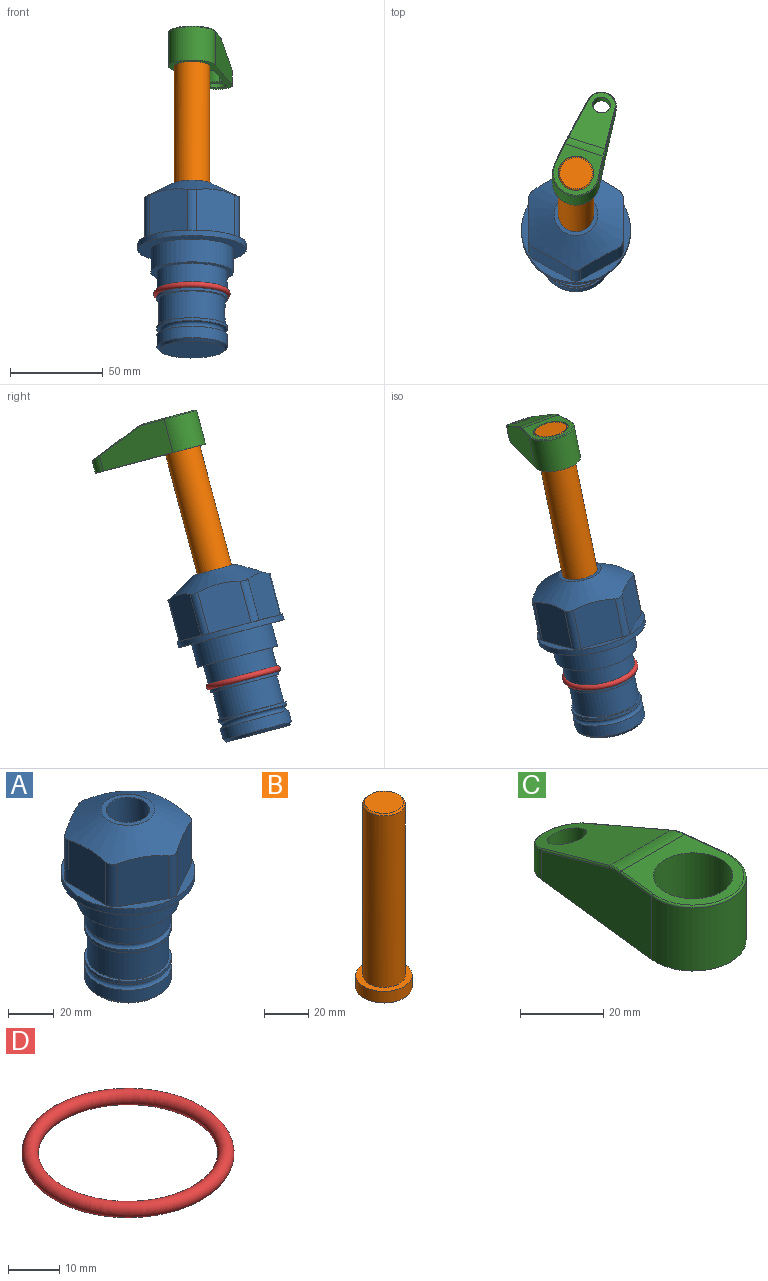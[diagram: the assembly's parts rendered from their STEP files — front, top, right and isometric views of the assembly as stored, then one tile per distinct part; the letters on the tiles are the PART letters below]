
ASSEMBLY  parts=4 mates=2
PART A: 36 faces, bbox 58.7x58.7x91.2 mm
  f0: cylinder r=17.78mm len=35.56mm, axis (0,0,1), area 1670.8mm2, adj f23,f24,f31
  f1: cylinder r=19.05mm len=38.1mm, axis (0,0,1), area 1191.9mm2, adj f26,f27,f30
  f2: plane 58.66x58.66mm, normal (0,0,-1), area 1150.6mm2, adj f3,f28
  f3: cylinder r=29.33mm len=58.66mm, axis (0,0,-1), area 585.1mm2, adj f2,f4
  f4: plane 58.66x58.66mm, normal (0,0,1), area 475.9mm2, adj f3,f5,f6,f7,f8,f9,f10,f11
  f5: plane 24.5x20.32mm, normal (-0.5,0.87,0), area 562.8mm2, adj f4,f15,f16,f17
  f6: plane 24.5x20.32mm, normal (0.5,0.87,0), area 562.8mm2, adj f4,f14,f15,f17
  f7: plane 24.5x23.48mm, normal (1,0,0), area 562.8mm2, adj f4,f13,f14,f17
  f8: plane 24.5x20.32mm, normal (0.5,-0.87,0), area 562.8mm2, adj f4,f12,f13,f17
  f9: plane 24.5x20.32mm, normal (-0.5,-0.87,0), area 562.8mm2, adj f4,f11,f12,f17
  f10: plane 24.5x23.48mm, normal (-1,0,0), area 562.8mm2, adj f4,f11,f16,f17
  f11: cylinder r=5.08mm len=23.01mm, axis (0,0,-1), area 121.2mm2, adj f4,f9,f10,f17
  f12: cylinder r=5.08mm len=23.01mm, axis (0,0,-1), area 121.2mm2, adj f4,f8,f9,f17
  f13: cylinder r=5.08mm len=23.01mm, axis (0,0,-1), area 121.2mm2, adj f4,f7,f8,f17
  f14: cylinder r=5.08mm len=23.01mm, axis (0,0,-1), area 121.2mm2, adj f4,f6,f7,f17
  f15: cylinder r=5.08mm len=23.01mm, axis (0,0,-1), area 121.2mm2, adj f4,f5,f6,f17
  f16: cylinder r=5.08mm len=23.01mm, axis (0,0,-1), area 121.2mm2, adj f4,f5,f10,f17
  f17: cone r=11.73mm half-angle=60deg, axis (0,0,-1), area 2071.8mm2, adj f5,f6,f7,f8,f9,f10,f11,f12
  f18: plane 23.46x23.46mm, normal (0,0,1), area 147.4mm2, adj f17,f35
  f19: plane 34.93x34.93mm, normal (0,0,-1), area 958mm2, adj f29
  f20: cylinder r=19.05mm len=38.1mm, axis (0,0,1), area 760.1mm2, adj f21,f29
  f21: torus R=19.05mm, axis (0,0,1), area 565.3mm2, adj f20,f22
  f22: cylinder r=19.05mm len=38.1mm, axis (0,0,1), area 190mm2, adj f21,f23
  f23: plane 38.1x38.1mm, normal (0,0,1), area 146.9mm2, adj f0,f22
  f24: plane 38.1x38.1mm, normal (0,0,-1), area 146.9mm2, adj f0,f25
  f25: cylinder r=19.05mm len=38.1mm, axis (0,0,1), area 190mm2, adj f24,f26
  f26: torus R=19.05mm, axis (0,0,1), area 565.3mm2, adj f1,f25
  f27: plane 44.45x44.45mm, normal (0,0,-1), area 411.7mm2, adj f1,f28
  f28: cylinder r=22.23mm len=44.45mm, axis (0,0,1), area 1773.5mm2, adj f2,f27
  f29: cone r=19.05mm half-angle=45deg, axis (0,0,1), area 257.5mm2, adj f19,f20
  f30: cylinder r=3.17mm len=6.75mm, axis (-1,0,0), area 128mm2, adj f1,f33
  f31: cylinder r=3.17mm len=6.35mm, axis (-1,0,0), area 102.5mm2, adj f0,f33
  f32: plane 25.4x25.4mm, normal (0,0,1), area 506.7mm2, adj f33
  f33: cylinder r=12.7mm len=66.42mm, axis (0,0,-1), area 5236.2mm2, adj f30,f31,f32,f34
  f34: cone r=9.53mm half-angle=30deg, axis (0,0,-1), area 443.4mm2, adj f33,f35
  f35: cylinder r=9.53mm len=19.05mm, axis (0,0,-1), area 849mm2, adj f18,f34
PART B: 6 faces, bbox 25.4x25.4x101.6 mm
  f0: plane 17.46x17.46mm, normal (0,0,1), area 239.5mm2, adj f5
  f1: plane 25.4x25.4mm, normal (0,0,-1), area 506.7mm2, adj f2
  f2: cylinder r=12.7mm len=25.4mm, axis (0,0,1), area 506.7mm2, adj f1,f3
  f3: plane 25.4x25.4mm, normal (0,0,1), area 221.7mm2, adj f2,f4
  f4: cylinder r=9.53mm len=94.46mm, axis (0,0,1), area 5653mm2, adj f3,f5
  f5: cone r=8.73mm half-angle=45deg, axis (0,0,-1), area 64.4mm2, adj f0,f4
PART C: 44 faces, bbox 27.5x64.5x19.1 mm
  f0: plane 2.3x0.95mm, normal (0,0,-1), area 1mm2, adj f25,f30,f34
  f1: plane 63.5x25.4mm, normal (0,0,-1), area 561.7mm2, adj f2,f3,f4,f5,f6,f7,f19,f20
  f2: cylinder r=12.7mm len=25.4mm, axis (0,0,-1), area 792.2mm2, adj f1,f3,f5,f13
  f3: plane 42.33x18.54mm, normal (0.99,0.11,0), area 647mm2, adj f1,f2,f4,f11,f12,f14
  f4: cylinder r=7.94mm len=15.78mm, axis (0,0,-1), area 158.6mm2, adj f1,f3,f5,f16
  f5: plane 42.33x18.54mm, normal (-0.99,0.11,0), area 647mm2, adj f1,f2,f4,f15,f17,f18
  f6: cylinder r=9.53mm len=19.05mm, axis (0,0,-1), area 1140.1mm2, adj f1,f8
  f7: cylinder r=4.76mm len=10.98mm, axis (0,0,-1), area 276.1mm2, adj f1,f9
  f8: plane 25.83x24.38mm, normal (0,0,1), area 262.2mm2, adj f6,f10,f11,f13,f15
  f9: plane 32.49x20.55mm, normal (0,0.34,0.94), area 489.9mm2, adj f7,f10,f14,f16,f18
  f10: cylinder r=12.7mm len=21.49mm, axis (-1,0,0), area 93.2mm2, adj f8,f9,f12,f17
  f11: cylinder r=0.51mm len=12.34mm, axis (0.11,-0.99,0), area 9.9mm2, adj f3,f8,f12,f13
  f12: bspline ~7.62x1.64mm, area 3.5mm2, adj f3,f10,f11,f14
  f13: torus R=12.19mm, axis (0,0,1), area 33.6mm2, adj f2,f8,f11,f15
  f14: cylinder r=0.51mm len=26.01mm, axis (0.1,-0.93,0.34), area 21.6mm2, adj f3,f9,f12,f16
  f15: cylinder r=0.51mm len=12.34mm, axis (0.11,0.99,0), area 9.9mm2, adj f5,f8,f13,f17
  f16: bspline ~15.78x7.05mm, area 15.7mm2, adj f4,f9,f14,f18
  f17: bspline ~7.62x1.64mm, area 3.5mm2, adj f5,f10,f15,f18
  f18: cylinder r=0.51mm len=26.01mm, axis (0.1,0.93,-0.34), area 21.6mm2, adj f5,f9,f16,f17
  f19: plane 21.6x14.29mm, normal (-0.99,-0.11,0), area 242.6mm2, adj f1,f26,f28,f34,f36,f38
  f20: plane 21.6x14.29mm, normal (0.99,-0.11,0), area 242.6mm2, adj f1,f27,f29,f37,f39,f41
  f21: cylinder r=12.7mm len=14.29mm, axis (0,0,-1), area 173.2mm2, adj f1,f26,f27,f30,f31,f33
  f22: cylinder r=7.94mm len=7.63mm, axis (0,0,-1), area 53.8mm2, adj f1,f28,f29,f42
  f23: plane 2.3x0.95mm, normal (0,0,-1), area 1mm2, adj f25,f33,f37
  f24: plane 17.94x12.32mm, normal (0,-0.34,-0.94), area 191.2mm2, adj f25,f38,f41,f42
  f25: cylinder r=9.53mm len=12.93mm, axis (-1,0,0), area 37.5mm2, adj f0,f23,f24,f31,f36,f39
  f26: cylinder r=1.59mm len=14.29mm, axis (0,0,-1), area 49mm2, adj f1,f19,f21,f32
  f27: cylinder r=1.59mm len=14.29mm, axis (0,0,-1), area 49mm2, adj f1,f20,f21,f35
  f28: cylinder r=1.59mm len=7.28mm, axis (0,0,-1), area 22.1mm2, adj f1,f19,f22,f40
  f29: cylinder r=1.59mm len=7.28mm, axis (0,0,-1), area 22.1mm2, adj f1,f20,f22,f43
  f30: torus R=14.29mm, axis (0,0,1), area 5.8mm2, adj f0,f21,f31,f32
  f31: bspline ~11.06x2.73mm, area 20.8mm2, adj f21,f25,f30,f33
  f32: sphere r=1.59mm, area 5.4mm2, adj f26,f30,f34
  f33: torus R=14.29mm, axis (0,0,1), area 5.8mm2, adj f21,f23,f31,f35
  f34: cylinder r=1.59mm len=1.68mm, axis (-0.11,0.99,0), area 2.4mm2, adj f0,f19,f32,f36
  f35: sphere r=1.59mm, area 5.4mm2, adj f27,f33,f37
  f36: bspline ~5.82x2.33mm, area 7.7mm2, adj f19,f25,f34,f38
  f37: cylinder r=1.59mm len=1.68mm, axis (0.11,0.99,0), area 2.4mm2, adj f20,f23,f35,f39
  f38: cylinder r=1.59mm len=18.33mm, axis (0.1,-0.93,0.34), area 46.7mm2, adj f19,f24,f36,f40
  f39: bspline ~5.82x2.33mm, area 7.7mm2, adj f20,f25,f37,f41
  f40: sphere r=1.59mm, area 3.6mm2, adj f28,f38,f42
  f41: cylinder r=1.59mm len=18.33mm, axis (0.1,0.93,-0.34), area 46.7mm2, adj f20,f24,f39,f43
  f42: bspline ~8.31x1.84mm, area 15.3mm2, adj f22,f24,f40,f43
  f43: sphere r=1.59mm, area 3.6mm2, adj f29,f41,f42
PART D: 1 faces, bbox 44.7x44.7x3.2 mm
  f0: torus R=19.05mm, axis (0,0,1), area 1193.9mm2
PLACE A rot(axis=(-1,0,0),14.9deg) t=(-16.98,4.37,-41.54)mm
PLACE B rot(axis=(-0.62,-0.1,-0.78),23.8deg) t=(-16.98,16.61,4.46)mm
PLACE C rot(axis=(-0.62,-0.1,-0.78),23.8deg) t=(-16.98,30.64,57.23)mm
PLACE D rot(axis=(-1,0,0),14.9deg) t=(-16.98,4.37,-41.54)mm
MATE fastened C.f2 <-> B.f2  axis (0,-0.26,-0.97) through (-16.98,35.54,75.64)mm
MATE cylindrical B.f2 <-> A.f0  axis (0,0.26,0.97) through (-16.98,23.2,29.24)mm
